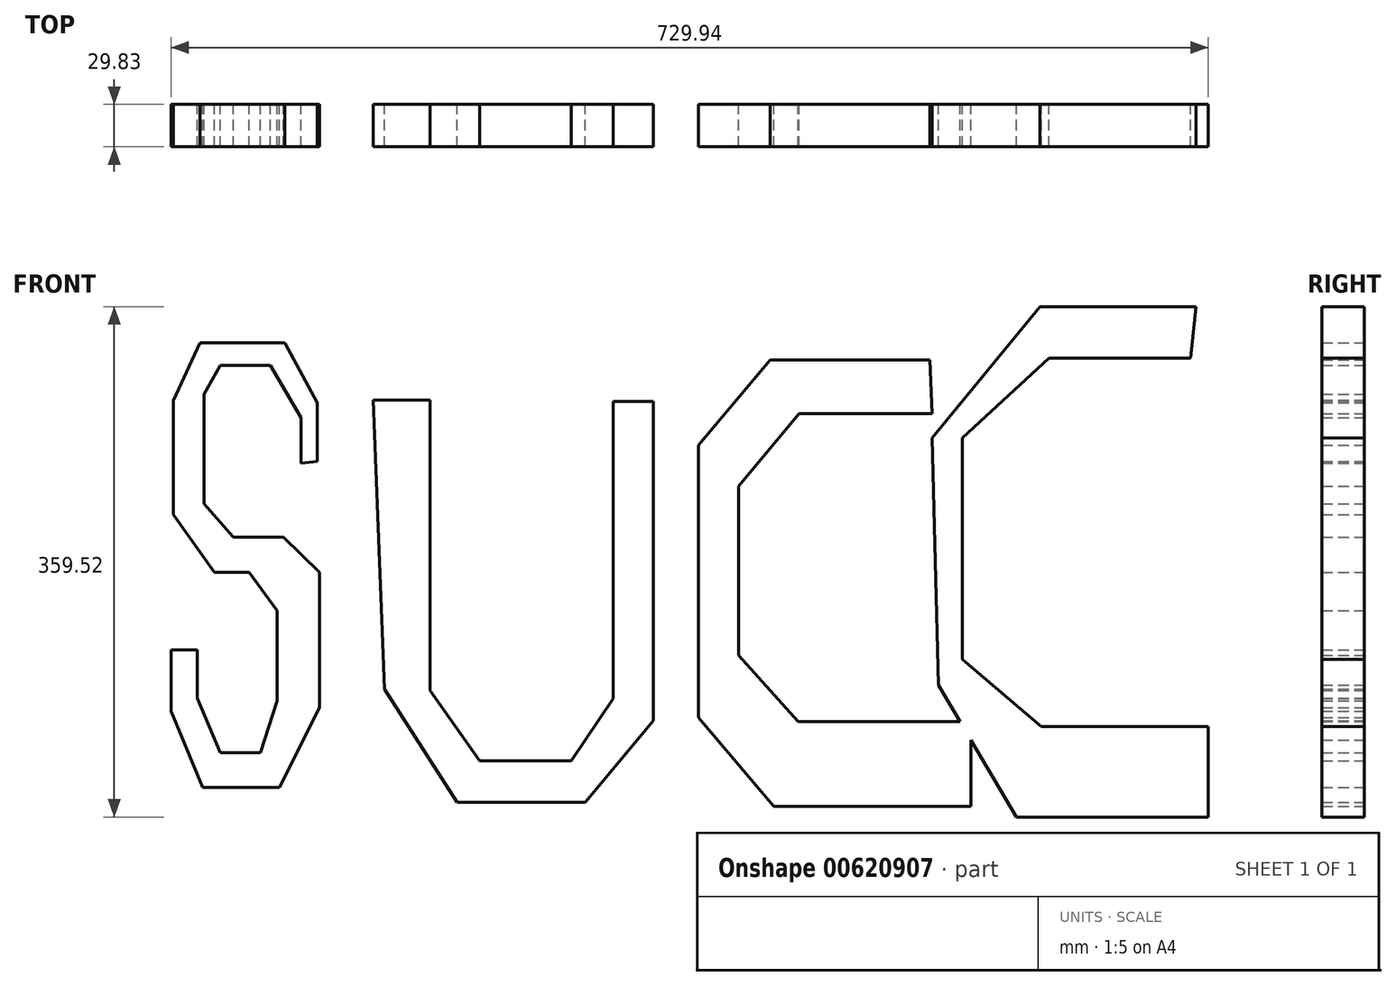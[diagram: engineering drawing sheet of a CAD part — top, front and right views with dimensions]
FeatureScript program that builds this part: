
annotation { "Feature Type Name" : "Feature", "Feature Type Description" : "" }
export const myFeature = defineFeature(function(context is Context, id is Id, definition is map)
    precondition{}
    {
        {
            var Q0;
            Q0=qCreatedBy(makeId("Front.planeOp"),FACE);
            var sketch = newSketch(context, id + "F0", { "sketchPlane" : qUnion([Q0])});
            skLineSegment(sketch, "E0", {"start": v(-137.06, 78.17) * mm, "end": v(-137.06, 119.28) * mm});
            skLineSegment(sketch, "E1", {"start": v(-137.06, 119.28) * mm, "end": v(-159.94, 161.46) * mm});
            skLineSegment(sketch, "E2", {"start": v(-159.94, 161.46) * mm, "end": v(-219.63, 161.46) * mm});
            skLineSegment(sketch, "E3", {"start": v(-219.63, 161.46) * mm, "end": v(-238.22, 121.06) * mm});
            skLineSegment(sketch, "E4", {"start": v(-238.22, 121.06) * mm, "end": v(-238.22, 40.64) * mm});
            skLineSegment(sketch, "E5", {"start": v(-238.22, 40.64) * mm, "end": v(-209.27, 0) * mm});
            skLineSegment(sketch, "E6", {"start": v(-209.27, 0) * mm, "end": v(-184.96, 0) * mm});
            skLineSegment(sketch, "E7", {"start": v(-184.96, 0) * mm, "end": v(-165.3, -26.92) * mm});
            skLineSegment(sketch, "E8", {"start": v(-165.3, -26.92) * mm, "end": v(-165.3, -90.54) * mm});
            skLineSegment(sketch, "E9", {"start": v(-165.3, -90.54) * mm, "end": v(-177.1, -127) * mm});
            skLineSegment(sketch, "E10", {"start": v(-177.1, -127) * mm, "end": v(-205.29, -127) * mm});
            skLineSegment(sketch, "E11", {"start": v(-205.29, -127) * mm, "end": v(-221.31, -88.53) * mm});
            skLineSegment(sketch, "E12", {"start": v(-221.31, -88.53) * mm, "end": v(-221.31, -54.7) * mm});
            skLineSegment(sketch, "E13", {"start": v(-221.31, -54.7) * mm, "end": v(-239.83, -54.7) * mm});
            skLineSegment(sketch, "E14", {"start": v(-239.83, -54.7) * mm, "end": v(-239.83, -97.8) * mm});
            skLineSegment(sketch, "E15", {"start": v(-239.83, -97.8) * mm, "end": v(-217.47, -151.62) * mm});
            skLineSegment(sketch, "E16", {"start": v(-217.47, -151.62) * mm, "end": v(-177.84, -151.62) * mm});
            skLineSegment(sketch, "E17", {"start": v(-177.84, -151.62) * mm, "end": v(-163.56, -151.62) * mm});
            skLineSegment(sketch, "E18", {"start": v(-163.56, -151.62) * mm, "end": v(-135.36, -95.22) * mm});
            skLineSegment(sketch, "E19", {"start": v(-135.36, -95.22) * mm, "end": v(-135.36, 0) * mm});
            skLineSegment(sketch, "E20", {"start": v(-135.36, 0) * mm, "end": v(-160.7, 24.72) * mm});
            skLineSegment(sketch, "E21", {"start": v(-160.7, 24.72) * mm, "end": v(-196.05, 24.72) * mm});
            skLineSegment(sketch, "E22", {"start": v(-196.05, 24.72) * mm, "end": v(-216.75, 48.28) * mm});
            skLineSegment(sketch, "E23", {"start": v(-216.75, 48.28) * mm, "end": v(-216.75, 125.4) * mm});
            skLineSegment(sketch, "E24", {"start": v(-216.75, 125.4) * mm, "end": v(-205.33, 145.74) * mm});
            skLineSegment(sketch, "E25", {"start": v(-205.33, 145.74) * mm, "end": v(-169.99, 145.74) * mm});
            skLineSegment(sketch, "E26", {"start": v(-169.99, 145.74) * mm, "end": v(-148.5, 108.97) * mm});
            skPoint(sketch, "E26.endSnap0", {"position": v(-148.5, 140.37) * mm});
            skLineSegment(sketch, "E27", {"start": v(-148.5, 108.97) * mm, "end": v(-148.5, 76.84) * mm});
            skLineSegment(sketch, "E28", {"start": v(-148.5, 76.84) * mm, "end": v(-137.06, 78.17) * mm});
            skLineSegment(sketch, "E29", {"start": v(-97.52, 121.1) * mm, "end": v(-57.54, 121.1) * mm});
            skLineSegment(sketch, "E30", {"start": v(-57.54, 121.1) * mm, "end": v(-57.54, -83.08) * mm});
            skLineSegment(sketch, "E31", {"start": v(-57.54, -83.08) * mm, "end": v(-22.56, -132.7) * mm});
            skLineSegment(sketch, "E32", {"start": v(-22.56, -132.7) * mm, "end": v(41.7, -132.7) * mm});
            skLineSegment(sketch, "E33", {"start": v(41.7, -132.7) * mm, "end": v(71.33, -88.8) * mm});
            skLineSegment(sketch, "E34", {"start": v(71.33, -88.8) * mm, "end": v(71.33, 120.4) * mm});
            skLineSegment(sketch, "E35", {"start": v(71.33, 120.4) * mm, "end": v(99.53, 120.4) * mm});
            skLineSegment(sketch, "E36", {"start": v(99.53, 120.4) * mm, "end": v(99.53, -104.5) * mm});
            skLineSegment(sketch, "E37", {"start": v(99.53, -104.5) * mm, "end": v(51.7, -161.98) * mm});
            skLineSegment(sketch, "E38", {"start": v(51.7, -161.98) * mm, "end": v(-38.62, -161.98) * mm});
            skLineSegment(sketch, "E39", {"start": v(-38.62, -161.98) * mm, "end": v(-89.67, -82.37) * mm});
            skLineSegment(sketch, "E40", {"start": v(-89.67, -82.37) * mm, "end": v(-97.52, 121.1) * mm});
            skLineSegment(sketch, "E41", {"start": v(294.29, 149.64) * mm, "end": v(181.81, 149.64) * mm});
            skLineSegment(sketch, "E42", {"start": v(181.81, 149.64) * mm, "end": v(131.34, 89.55) * mm});
            skLineSegment(sketch, "E43", {"start": v(131.34, 89.55) * mm, "end": v(131.34, -102.24) * mm});
            skLineSegment(sketch, "E44", {"start": v(131.34, -102.24) * mm, "end": v(184.22, -164.72) * mm});
            skLineSegment(sketch, "E45", {"start": v(184.22, -164.72) * mm, "end": v(323.13, -164.72) * mm});
            skLineSegment(sketch, "E46", {"start": v(323.13, -164.72) * mm, "end": v(323.13, -105.12) * mm});
            skLineSegment(sketch, "E47", {"start": v(323.13, -105.12) * mm, "end": v(201.52, -105.12) * mm});
            skLineSegment(sketch, "E48", {"start": v(201.52, -105.12) * mm, "end": v(159.7, -58.5) * mm});
            skLineSegment(sketch, "E49", {"start": v(159.7, -58.5) * mm, "end": v(159.7, 60.71) * mm});
            skLineSegment(sketch, "E50", {"start": v(159.7, 60.71) * mm, "end": v(202, 111.66) * mm});
            skLineSegment(sketch, "E51", {"start": v(202, 111.66) * mm, "end": v(295.73, 111.66) * mm});
            skLineSegment(sketch, "E52", {"start": v(295.73, 111.66) * mm, "end": v(294.29, 149.64) * mm});
            skLineSegment(sketch, "E53", {"start": v(477.6, 150.69) * mm, "end": v(378.06, 150.69) * mm});
            skLineSegment(sketch, "E54", {"start": v(378.06, 150.69) * mm, "end": v(317.15, 94.67) * mm});
            skLineSegment(sketch, "E55", {"start": v(317.15, 94.67) * mm, "end": v(317.15, -61.43) * mm});
            skLineSegment(sketch, "E56", {"start": v(317.15, -61.43) * mm, "end": v(372.63, -108.75) * mm});
            skLineSegment(sketch, "E57", {"start": v(372.63, -108.75) * mm, "end": v(490.1, -108.75) * mm});
            skLineSegment(sketch, "E58", {"start": v(490.1, -108.75) * mm, "end": v(490.1, -172.39) * mm});
            skLineSegment(sketch, "E59", {"start": v(490.1, -172.39) * mm, "end": v(355.22, -172.39) * mm});
            skLineSegment(sketch, "E60", {"start": v(355.22, -172.39) * mm, "end": v(300.29, -79.38) * mm});
            skLineSegment(sketch, "E61", {"start": v(300.29, -79.38) * mm, "end": v(295.73, 94.67) * mm});
            skLineSegment(sketch, "E62", {"start": v(295.73, 94.67) * mm, "end": v(371.54, 187.13) * mm});
            skLineSegment(sketch, "E63", {"start": v(371.54, 187.13) * mm, "end": v(481.4, 187.13) * mm});
            skLineSegment(sketch, "E64", {"start": v(481.4, 187.13) * mm, "end": v(477.6, 150.69) * mm});
            skSolve(sketch);
        }
        {
            var Q0;
            Q0 = qSketchRegion(id + "F0", true);
            extrude(context, id + "F1", {"entities" : qUnion([Q0]), "depth" : 29.83 * mm, "offsetDistance" : 25.4 * mm});
        }
    });
